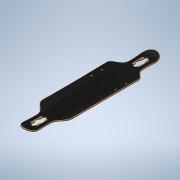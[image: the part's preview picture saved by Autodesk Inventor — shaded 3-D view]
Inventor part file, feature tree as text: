
AUTODESK INVENTOR PART (.ipt)
format: ipt  version: 2020.1 (Build 241239000, 239)  size: 6,141,440 bytes
history: native  units: in
note: dims shown in document units (in); Inventor stores cm internally (conversion verified against a paired STEP export)
features: other x12, sketch x6, extrude x6, reference x4, plane x2, loft x1, fillet x1, chamfer x1
ambient origin geometry x8: Origin, YZ Plane, XZ Plane, XY Plane, X Axis, Y Axis, Z Axis, Center Point
bodies: Body1 (feature_tree)
feature tree (33):
  sketch  "Sketch1"  dims[d113=9.6457in d114=40.748in]
  sketch  "Sketch2"  dims[d154=3.937in d155=40.748in d180=4.8228in]
  sketch  "Sketch3"  dims[d181=3.937in d183=9.6457in]
  other  "Bottom Profile"
  other  "Front Profile"
  other  "Front Profile Projection Plane"
  other  "Front Profile Projection"
  other  "Side Profile"
  loft  "Board Loft"
  extrude  "Shape Extrusion"  Depth=40.748in
  fillet  "Fillet6"  Radius=4.8228in
  plane  "Work Plane11"
  sketch  "Sketch26"  dims[d354=0.2165in d355=0.2165in]
  extrude  "Extrusion15"  Depth=9.6457in
  extrude  "Extrusion17"  Depth=0.2165in
  plane  "Work Plane12"
  sketch  "Sketch27"  dims[d356=20.374in d357=20.374in d378=2.126in d379=2.5in d384=0.9843in d394=0.5512in d395=180.0deg d396=0.5512in d397=180.0deg d400=0.7874in d401=0.3937in d402=3.3071in d403=0.7874in d404=0.5118in d408=5.9055in d409=0.0984in d410=0.0984in d412=90.0deg d413=5.9055in d414=0.3937in d415=0.3937in d417=0.3937in d421=0.3937in d563=2.0079in d564=0.0in d577=0.0055in d578=3.7205in d579=0.0055in d580=3.7205in d582=3.2087in d583=3.2087in d584=4.0197in d585=4.0197in d586=3.1969in d587=3.1969in d588=0.0in d589=0.0in d596=0.0in d597=90.0deg d598=0.0in d599=90.0deg d600=0.0in d601=90.0deg d602=14.4454in d603=0.0in d606=0.4724in d607=0.4724in d608=0.0039in d609=0.0in d610=0.4724in d612=0.4724in d613=0.0039in d614=0.0in d615=0.0039in d616=0.0in d617=0.0039in d618=0.0in d619=0.0787in d620=0.1181in d629=0.1181in d630=0.0787in d631=45.0deg]
  extrude  "Extrusion16"  Depth=0.2165in
  extrude  "Extrusion18"  Depth=20.374in
  extrude  "Extrusion12"  Depth=2.126in
  chamfer  "Chamfer2"  Distance=2.5in
  other  "Image4"
  other  "Image5"
  other  "Image6"
  sketch  "Sketch25"  dims[d350=0.813in d353=0.2165in]
  reference  "Reference1"
  reference  "Reference2"
  reference  "Reference3"
  reference  "Reference4"
  parser-record x1  (decoder bookkeeping rows leaked as tree rows — omitted from the tree; the rows remain in map.json)
  other  "Longboard.iam"
  other  "Housing v3:1"
  other  "Battery Housing Box v3:1"
note: 1 file-system path scrubbed to <path> (originals preserved in map.json)
